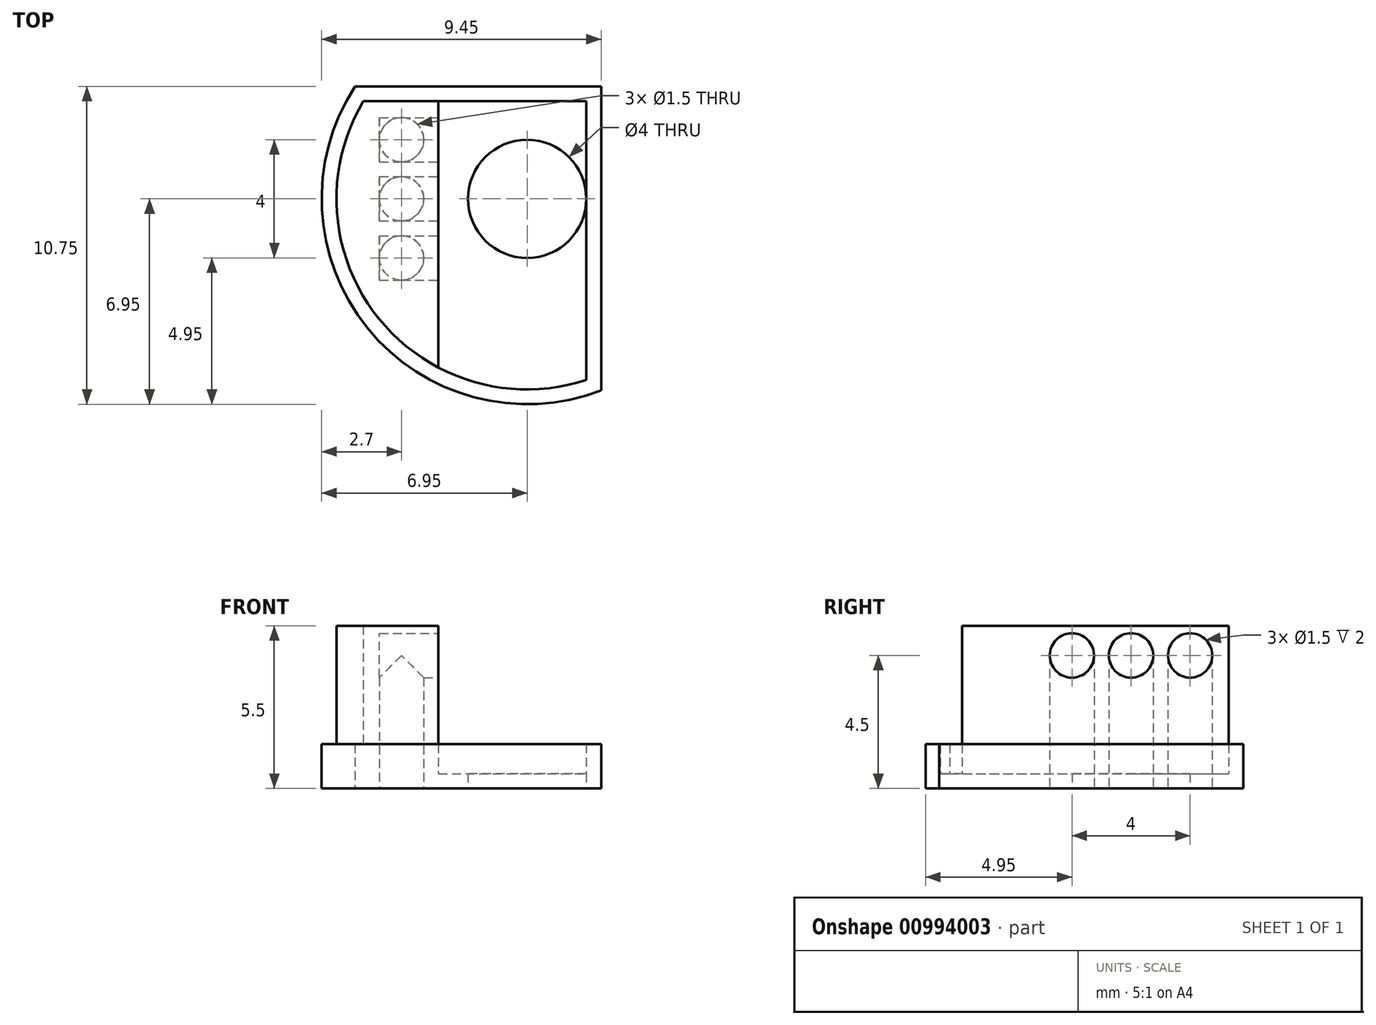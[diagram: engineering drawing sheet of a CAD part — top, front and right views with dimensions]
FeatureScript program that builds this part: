
annotation { "Feature Type Name" : "Feature", "Feature Type Description" : "" }
export const myFeature = defineFeature(function(context is Context, id is Id, definition is map)
    precondition{}
    {
        {
            var Q0;
            Q0=qCreatedBy(makeId("Top.planeOp"),FACE);
            var sketch = newSketch(context, id + "F0", { "sketchPlane" : qUnion([Q0])});
            skCircle(sketch, "E0", {"center": v(0, 0) * mm, "radius": 6.95 * mm});
            skCircle(sketch, "E1", {"center": v(0, 0) * mm, "radius": 6.45 * mm});
            skCircle(sketch, "E2", {"center": v(0, 0) * mm, "radius": 2 * mm});
            skLineSegment(sketch, "E3", {"start": v(5.82, 3.8) * mm, "end": v(-5.82, 3.8) * mm});
            skLineSegment(sketch, "E4", {"start": v(2.5, 6.48) * mm, "end": v(2.5, -6.48) * mm});
            skLineSegment(sketch, "E5", {"start": v(5.54, 3.3) * mm, "end": v(-5.54, 3.3) * mm});
            skLineSegment(sketch, "E6", {"start": v(-3, 6.27) * mm, "end": v(-3, -6.27) * mm});
            skLineSegment(sketch, "E7", {"start": v(2, 6.66) * mm, "end": v(2, -6.66) * mm});
            skSolve(sketch);
        }
        {
            var Q0;
            {var subQ5=sQuery(id+"F0.wireOp",EDGE,"E3");var subQ7=sQuery(id+"F0.wireOp",EDGE,"E0");var subQ8=makeQuery(id+"F0.imprint","INTERSECT",VERTEX,{"disambiguationData":[OD(1.0)],"derivedFrom":[subQ7,subQ5]});Q0=makeQuery(id+"F0.imprint","IMPRINT",FACE,{"disambiguationData":[TD([[makeQuery(id+"F0.imprint","IMPRINT",EDGE,{"disambiguationData":[TD([[subQ8,-1.0]])],"derivedFrom":subQ7}),1.0]])]});}
            var Q1;
            {var subQ0=sQuery(id+"F0.wireOp",EDGE,"E5");var subQ1=sQuery(id+"F0.wireOp",EDGE,"E1");var subQ2=makeQuery(id+"F0.imprint","INTERSECT",VERTEX,{"disambiguationData":[OD(1.0)],"derivedFrom":[subQ1,subQ0]});Q1=makeQuery(id+"F0.imprint","IMPRINT",FACE,{"disambiguationData":[TD([[makeQuery(id+"F0.imprint","IMPRINT",EDGE,{"disambiguationData":[TD([[subQ2,1.0]])],"derivedFrom":subQ1}),1.0]])]});}
            var Q2;
            {var subQ0=sQuery(id+"F0.wireOp",EDGE,"E4");var subQ1=sQuery(id+"F0.wireOp",EDGE,"E3");var subQ2=makeQuery(id+"F0.imprint","INTERSECT",VERTEX,{"derivedFrom":[subQ1,subQ0]});Q2=makeQuery(id+"F0.imprint","IMPRINT",FACE,{"disambiguationData":[TD([[makeQuery(id+"F0.imprint","IMPRINT",EDGE,{"disambiguationData":[TD([[subQ2,-1.0]])],"derivedFrom":subQ1}),1.0]])]});}
            var Q3;
            {var subQ0=sQuery(id+"F0.wireOp",EDGE,"3qxJMtrC-riru-1C9R-vTC9-Mj8YmDp8AXd7");var subQ1=sQuery(id+"F0.wireOp",EDGE,"E1");var subQ2=makeQuery(id+"F0.imprint","INTERSECT",VERTEX,{"disambiguationData":[OD(1.0)],"derivedFrom":[subQ1,subQ0]});Q3=makeQuery(id+"F0.imprint","IMPRINT",FACE,{"disambiguationData":[TD([[makeQuery(id+"F0.imprint","IMPRINT",EDGE,{"disambiguationData":[TD([[subQ2,-1.0]])],"derivedFrom":subQ1}),1.0]])]});}
            var Q4;
            {var subQ0=sQuery(id+"F0.wireOp",EDGE,"E5");var subQ1=sQuery(id+"F0.wireOp",EDGE,"E1");var subQ2=makeQuery(id+"F0.imprint","INTERSECT",VERTEX,{"disambiguationData":[OD(1.0)],"derivedFrom":[subQ1,subQ0]});Q4=makeQuery(id+"F0.imprint","IMPRINT",FACE,{"disambiguationData":[TD([[makeQuery(id+"F0.imprint","IMPRINT",EDGE,{"disambiguationData":[TD([[subQ2,-1.0]])],"derivedFrom":subQ1}),1.0]])]});}
            var Q5;
            {var subQ0=sQuery(id+"F0.wireOp",EDGE,"E4");var subQ1=sQuery(id+"F0.wireOp",EDGE,"E0");var subQ2=makeQuery(id+"F0.imprint","INTERSECT",VERTEX,{"disambiguationData":[OD(1.0)],"derivedFrom":[subQ1,subQ0]});Q5=makeQuery(id+"F0.imprint","IMPRINT",FACE,{"disambiguationData":[TD([[makeQuery(id+"F0.imprint","IMPRINT",EDGE,{"disambiguationData":[TD([[subQ2,1.0]])],"derivedFrom":subQ1}),1.0]])]});}
            var Q6;
            Q6=makeQuery(id+"F0.imprint","IMPRINT",FACE,{"disambiguationData":[TD([[makeQuery(id+"F0.imprint","IMPRINT",EDGE,{"derivedFrom":sQuery(id+"F0.wireOp",EDGE,"E2")}),-1.0]])]});
            var Q7;
            {var subQ0=sQuery(id+"F0.wireOp",EDGE,"E7");var subQ6=sQuery(id+"F0.wireOp",EDGE,"E1");var subQ8=makeQuery(id+"F0.imprint","INTERSECT",VERTEX,{"disambiguationData":[OD(1.0)],"derivedFrom":[subQ6,subQ0]});Q7=makeQuery(id+"F0.imprint","IMPRINT",FACE,{"disambiguationData":[TD([[makeQuery(id+"F0.imprint","IMPRINT",EDGE,{"disambiguationData":[TD([[subQ8,-1.0]])],"derivedFrom":subQ6}),1.0]])]});}
            var Q8;
            {var subQ0=sQuery(id+"F0.wireOp",EDGE,"E7");var subQ1=sQuery(id+"F0.wireOp",EDGE,"E3");var subQ2=makeQuery(id+"F0.imprint","INTERSECT",VERTEX,{"derivedFrom":[subQ1,subQ0]});Q8=makeQuery(id+"F0.imprint","IMPRINT",FACE,{"disambiguationData":[TD([[makeQuery(id+"F0.imprint","IMPRINT",EDGE,{"disambiguationData":[TD([[subQ2,-1.0]])],"derivedFrom":subQ1}),1.0]])]});}
            var Q9;
            {var subQ0=sQuery(id+"F0.wireOp",EDGE,"E6");var subQ1=sQuery(id+"F0.wireOp",EDGE,"E0");var subQ2=makeQuery(id+"F0.imprint","INTERSECT",VERTEX,{"disambiguationData":[OD(1.0)],"derivedFrom":[subQ1,subQ0]});Q9=makeQuery(id+"F0.imprint","IMPRINT",FACE,{"disambiguationData":[TD([[makeQuery(id+"F0.imprint","IMPRINT",EDGE,{"disambiguationData":[TD([[subQ2,-1.0]])],"derivedFrom":subQ1}),1.0]])]});}
            extrude(context, id + "F1", {"entities" : qUnion([Q0, Q1, Q2, Q3, Q4, Q5, Q6, Q7, Q8, Q9]), "depth" : .5 * mm, "offsetDistance" : 25 * mm});
        }
        {
            var Q0;
            {var subQ0=sQuery(id+"F0.wireOp",EDGE,"E3");var subQ1=sQuery(id+"F0.wireOp",EDGE,"E0");var subQ2=makeQuery(id+"F0.imprint","INTERSECT",VERTEX,{"disambiguationData":[OD(1.0)],"derivedFrom":[subQ1,subQ0]});Q0=makeQuery(id+"F0.imprint","IMPRINT",FACE,{"disambiguationData":[TD([[makeQuery(id+"F0.imprint","IMPRINT",EDGE,{"disambiguationData":[TD([[subQ2,-1.0]])],"derivedFrom":subQ1}),1.0]])]});}
            var Q1;
            {var subQ0=sQuery(id+"F0.wireOp",EDGE,"E5");var subQ1=sQuery(id+"F0.wireOp",EDGE,"E1");var subQ2=makeQuery(id+"F0.imprint","INTERSECT",VERTEX,{"disambiguationData":[OD(1.0)],"derivedFrom":[subQ1,subQ0]});Q1=makeQuery(id+"F0.imprint","IMPRINT",FACE,{"disambiguationData":[TD([[makeQuery(id+"F0.imprint","IMPRINT",EDGE,{"disambiguationData":[TD([[subQ2,1.0]])],"derivedFrom":subQ1}),1.0]])]});}
            var Q2;
            {var subQ0=sQuery(id+"F0.wireOp",EDGE,"E4");var subQ1=sQuery(id+"F0.wireOp",EDGE,"E3");var subQ2=makeQuery(id+"F0.imprint","INTERSECT",VERTEX,{"derivedFrom":[subQ1,subQ0]});Q2=makeQuery(id+"F0.imprint","IMPRINT",FACE,{"disambiguationData":[TD([[makeQuery(id+"F0.imprint","IMPRINT",EDGE,{"disambiguationData":[TD([[subQ2,-1.0]])],"derivedFrom":subQ1}),1.0]])]});}
            var Q3;
            {var subQ0=sQuery(id+"F0.wireOp",EDGE,"E4");var subQ1=sQuery(id+"F0.wireOp",EDGE,"E0");var subQ2=makeQuery(id+"F0.imprint","INTERSECT",VERTEX,{"disambiguationData":[OD(1.0)],"derivedFrom":[subQ1,subQ0]});Q3=makeQuery(id+"F0.imprint","IMPRINT",FACE,{"disambiguationData":[TD([[makeQuery(id+"F0.imprint","IMPRINT",EDGE,{"disambiguationData":[TD([[subQ2,1.0]])],"derivedFrom":subQ1}),1.0]])]});}
            var Q4;
            {var subQ0=sQuery(id+"F0.wireOp",EDGE,"E6");var subQ1=sQuery(id+"F0.wireOp",EDGE,"E0");var subQ2=makeQuery(id+"F0.imprint","INTERSECT",VERTEX,{"disambiguationData":[OD(1.0)],"derivedFrom":[subQ1,subQ0]});Q4=makeQuery(id+"F0.imprint","IMPRINT",FACE,{"disambiguationData":[TD([[makeQuery(id+"F0.imprint","IMPRINT",EDGE,{"disambiguationData":[TD([[subQ2,-1.0]])],"derivedFrom":subQ1}),1.0]])]});}
            var Q5;
            {var subQ0=sQuery(id+"F0.wireOp",EDGE,"E7");var subQ6=sQuery(id+"F0.wireOp",EDGE,"E1");var subQ8=makeQuery(id+"F0.imprint","INTERSECT",VERTEX,{"disambiguationData":[OD(1.0)],"derivedFrom":[subQ6,subQ0]});Q5=makeQuery(id+"F0.imprint","IMPRINT",FACE,{"disambiguationData":[TD([[makeQuery(id+"F0.imprint","IMPRINT",EDGE,{"disambiguationData":[TD([[subQ8,-1.0]])],"derivedFrom":subQ6}),1.0]])]});}
            var Q6;
            {var subQ0=sQuery(id+"F0.wireOp",EDGE,"E7");var subQ1=sQuery(id+"F0.wireOp",EDGE,"E3");var subQ2=makeQuery(id+"F0.imprint","INTERSECT",VERTEX,{"derivedFrom":[subQ1,subQ0]});Q6=makeQuery(id+"F0.imprint","IMPRINT",FACE,{"disambiguationData":[TD([[makeQuery(id+"F0.imprint","IMPRINT",EDGE,{"disambiguationData":[TD([[subQ2,-1.0]])],"derivedFrom":subQ1}),1.0]])]});}
            extrude(context, id + "F2", {"entities" : qUnion([Q0, Q1, Q2, Q3, Q4, Q5, Q6]), "operationType" : NewBodyOperationType.ADD, "depth" : 1.5 * mm, "offsetDistance" : 25 * mm});
        }
        {
            var Q0;
            {var subQ0=sQuery(id+"F0.wireOp",EDGE,"E5");var subQ1=sQuery(id+"F0.wireOp",EDGE,"E1");var subQ2=makeQuery(id+"F0.imprint","INTERSECT",VERTEX,{"disambiguationData":[OD(1.0)],"derivedFrom":[subQ1,subQ0]});Q0=makeQuery(id+"F0.imprint","IMPRINT",FACE,{"disambiguationData":[TD([[makeQuery(id+"F0.imprint","IMPRINT",EDGE,{"disambiguationData":[TD([[subQ2,-1.0]])],"derivedFrom":subQ1}),1.0]])]});}
            extrude(context, id + "F3", {"entities" : qUnion([Q0]), "operationType" : NewBodyOperationType.ADD, "depth" : 5.5 * mm, "offsetDistance" : 25 * mm});
        }
        {
            var Q0;
            Q0=makeQuery(id+"F3.opExtrude","SWEPT_FACE",FACE,{"disambiguationData":[OSD([sQuery(id+"F0.wireOp",EDGE,"E6")])]});
            var sketch = newSketch(context, id + "F4", { "sketchPlane" : qUnion([Q0])});
            skLineSegment(sketch, "E8", {"start": v(0, 0) * mm, "end": v(0, 4.5) * mm});
            skLineSegment(sketch, "E9", {"start": v(0, 4.5) * mm, "end": v(-2, 4.5) * mm});
            skLineSegment(sketch, "E10", {"start": v(0, 4.5) * mm, "end": v(2, 4.5) * mm});
            skCircle(sketch, "E11", {"center": v(2, 4.5) * mm, "radius": 0.75 * mm});
            skCircle(sketch, "E12", {"center": v(0, 4.5) * mm, "radius": 0.75 * mm});
            skCircle(sketch, "E13", {"center": v(-2, 4.5) * mm, "radius": 0.75 * mm});
            skSolve(sketch);
        }
        {
            var Q0;
            Q0=makeQuery(id+"F4.imprint","IMPRINT",FACE,{"disambiguationData":[TD([[makeQuery(id+"F4.imprint","IMPRINT",EDGE,{"derivedFrom":sQuery(id+"F4.wireOp",EDGE,"E13")}),1.0]])]});
            var Q1;
            {var subQ1=sQuery(id+"F4.wireOp",EDGE,"E9");var subQ3=sQuery(id+"F4.wireOp",EDGE,"E12");var subQ4=makeQuery(id+"F4.imprint","INTERSECT",VERTEX,{"derivedFrom":[subQ1,subQ3]});Q1=makeQuery(id+"F4.imprint","IMPRINT",FACE,{"disambiguationData":[TD([[makeQuery(id+"F4.imprint","IMPRINT",EDGE,{"disambiguationData":[TD([[subQ4,1.0]])],"derivedFrom":subQ3}),1.0]])]});}
            var Q2;
            {var subQ1=sQuery(id+"F4.wireOp",EDGE,"E8");var subQ3=sQuery(id+"F4.wireOp",EDGE,"E12");var subQ4=makeQuery(id+"F4.imprint","INTERSECT",VERTEX,{"derivedFrom":[subQ1,subQ3]});Q2=makeQuery(id+"F4.imprint","IMPRINT",FACE,{"disambiguationData":[TD([[makeQuery(id+"F4.imprint","IMPRINT",EDGE,{"disambiguationData":[TD([[subQ4,1.0]])],"derivedFrom":subQ3}),1.0]])]});}
            var Q3;
            {var subQ1=sQuery(id+"F4.wireOp",EDGE,"E8");var subQ3=sQuery(id+"F4.wireOp",EDGE,"E12");var subQ4=makeQuery(id+"F4.imprint","INTERSECT",VERTEX,{"derivedFrom":[subQ1,subQ3]});Q3=makeQuery(id+"F4.imprint","IMPRINT",FACE,{"disambiguationData":[TD([[makeQuery(id+"F4.imprint","IMPRINT",EDGE,{"disambiguationData":[TD([[subQ4,-1.0]])],"derivedFrom":subQ3}),1.0]])]});}
            var Q4;
            Q4=makeQuery(id+"F4.imprint","IMPRINT",FACE,{"disambiguationData":[TD([[makeQuery(id+"F4.imprint","IMPRINT",EDGE,{"derivedFrom":sQuery(id+"F4.wireOp",EDGE,"E11")}),1.0]])]});
            var Q5;
            Q5=makeQuery(id+"F3.opExtrude","SWEPT_FACE",FACE,{"disambiguationData":[OSD([sQuery(id+"F0.wireOp",EDGE,"E1")])]});
            extrude(context, id + "F5", {"entities" : qUnion([Q0, Q1, Q2, Q3, Q4]), "operationType" : NewBodyOperationType.REMOVE, "oppositeDirection" : true, "depth" : 2 * mm, "endBoundEntityFace" : qUnion([Q5]), "offsetDistance" : 25 * mm});
        }
        {
            var Q0;
            Q0=qCreatedBy(makeId("Top.planeOp"),FACE);
            var sketch = newSketch(context, id + "F6", { "sketchPlane" : qUnion([Q0])});
            skLineSegment(sketch, "E14", {"start": v(0, 0) * mm, "end": v(-4.25, 0) * mm});
            skLineSegment(sketch, "E15", {"start": v(-4.25, 0) * mm, "end": v(-4.25, -2) * mm});
            skLineSegment(sketch, "E16", {"start": v(-4.25, 0) * mm, "end": v(-4.25, 2) * mm});
            skCircle(sketch, "E17", {"center": v(-4.25, 2) * mm, "radius": 0.75 * mm});
            skCircle(sketch, "E18", {"center": v(-4.25, 0) * mm, "radius": 0.75 * mm});
            skCircle(sketch, "E19", {"center": v(-4.25, -2) * mm, "radius": 0.75 * mm});
            skSolve(sketch);
        }
        {
            var Q0;
            Q0=makeQuery(id+"F6.imprint","IMPRINT",FACE,{"disambiguationData":[TD([[makeQuery(id+"F6.imprint","IMPRINT",EDGE,{"derivedFrom":sQuery(id+"F6.wireOp",EDGE,"E17")}),1.0]])]});
            var Q1;
            Q1=makeQuery(id+"F5.boolean.opBoolean","COPY",FACE,{"derivedFrom":makeQuery(id+"F5.opExtrude","SWEPT_FACE",FACE,{"disambiguationData":[OSD([sQuery(id+"F4.wireOp",EDGE,"E11")])]})});
            extrude(context, id + "F7", {"entities" : qUnion([Q0]), "operationType" : NewBodyOperationType.REMOVE, "endBound" : BoundingType.UP_TO_SURFACE, "depth" : 1.71 * mm, "endBoundEntityFace" : qUnion([Q1]), "offsetDistance" : 25 * mm});
        }
        {
            var Q0;
            {var subQ1=sQuery(id+"F6.wireOp",EDGE,"E14");var subQ3=sQuery(id+"F6.wireOp",EDGE,"E18");var subQ4=makeQuery(id+"F6.imprint","INTERSECT",VERTEX,{"derivedFrom":[subQ1,subQ3]});Q0=makeQuery(id+"F6.imprint","IMPRINT",FACE,{"disambiguationData":[TD([[makeQuery(id+"F6.imprint","IMPRINT",EDGE,{"disambiguationData":[TD([[subQ4,-1.0]])],"derivedFrom":subQ3}),1.0]])]});}
            var Q1;
            {var subQ1=sQuery(id+"F6.wireOp",EDGE,"E15");var subQ3=sQuery(id+"F6.wireOp",EDGE,"E18");var subQ4=makeQuery(id+"F6.imprint","INTERSECT",VERTEX,{"derivedFrom":[subQ1,subQ3]});Q1=makeQuery(id+"F6.imprint","IMPRINT",FACE,{"disambiguationData":[TD([[makeQuery(id+"F6.imprint","IMPRINT",EDGE,{"disambiguationData":[TD([[subQ4,1.0]])],"derivedFrom":subQ3}),1.0]])]});}
            var Q2;
            {var subQ1=sQuery(id+"F6.wireOp",EDGE,"E14");var subQ3=sQuery(id+"F6.wireOp",EDGE,"E18");var subQ4=makeQuery(id+"F6.imprint","INTERSECT",VERTEX,{"derivedFrom":[subQ1,subQ3]});Q2=makeQuery(id+"F6.imprint","IMPRINT",FACE,{"disambiguationData":[TD([[makeQuery(id+"F6.imprint","IMPRINT",EDGE,{"disambiguationData":[TD([[subQ4,1.0]])],"derivedFrom":subQ3}),1.0]])]});}
            var Q3;
            Q3=makeQuery(id+"F5.boolean.opBoolean","COPY",FACE,{"derivedFrom":makeQuery(id+"F5.opExtrude","SWEPT_FACE",FACE,{"disambiguationData":[OSD([sQuery(id+"F4.wireOp",EDGE,"E12")])]})});
            extrude(context, id + "F8", {"entities" : qUnion([Q0, Q1, Q2]), "operationType" : NewBodyOperationType.REMOVE, "endBound" : BoundingType.UP_TO_SURFACE, "depth" : 2.4 * mm, "endBoundEntityFace" : qUnion([Q3]), "offsetDistance" : 25 * mm});
        }
        {
            var Q0;
            Q0=makeQuery(id+"F6.imprint","IMPRINT",FACE,{"disambiguationData":[TD([[makeQuery(id+"F6.imprint","IMPRINT",EDGE,{"derivedFrom":sQuery(id+"F6.wireOp",EDGE,"E19")}),1.0]])]});
            var Q1;
            Q1=makeQuery(id+"F5.boolean.opBoolean","COPY",FACE,{"derivedFrom":makeQuery(id+"F5.opExtrude","SWEPT_FACE",FACE,{"disambiguationData":[OSD([sQuery(id+"F4.wireOp",EDGE,"E13")])]})});
            extrude(context, id + "F9", {"entities" : qUnion([Q0]), "operationType" : NewBodyOperationType.REMOVE, "endBound" : BoundingType.UP_TO_SURFACE, "depth" : 2.2 * mm, "endBoundEntityFace" : qUnion([Q1]), "offsetDistance" : 25 * mm});
        }
    });
